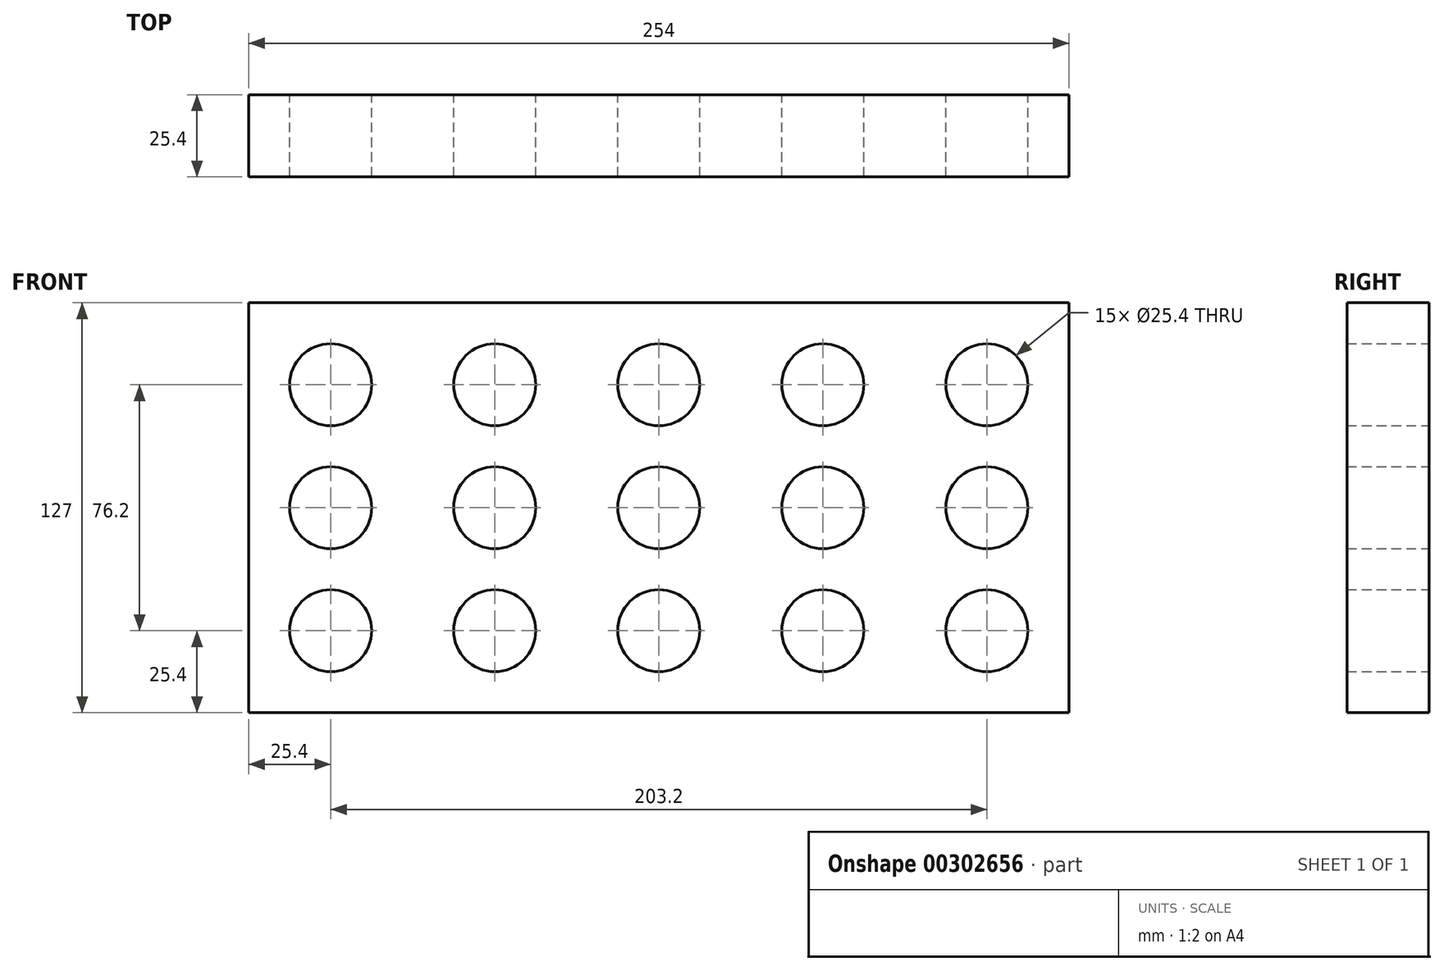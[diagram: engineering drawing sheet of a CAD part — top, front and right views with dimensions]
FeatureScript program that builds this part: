
annotation { "Feature Type Name" : "Feature", "Feature Type Description" : "" }
export const myFeature = defineFeature(function(context is Context, id is Id, definition is map)
    precondition{}
    {
        {
            var Q0;
            Q0=qCreatedBy(makeId("Front.planeOp"),FACE);
            var sketch = newSketch(context, id + "F0", { "sketchPlane" : qUnion([Q0])});
            skLineSegment(sketch, "E0.bottom", {"start": v(0, 0) * mm, "end": v(254, 0) * mm});
            skLineSegment(sketch, "E0.top", {"start": v(0, -127) * mm, "end": v(254, -127) * mm});
            skLineSegment(sketch, "E0.left", {"start": v(0, 0) * mm, "end": v(0, -127) * mm});
            skLineSegment(sketch, "E0.right", {"start": v(254, 0) * mm, "end": v(254, -127) * mm});
            skCircle(sketch, "E1", {"center": v(25.4, -25.4) * mm, "radius": 12.7 * mm});
            skCircle(sketch, "E2.0.1.0", {"center": v(25.4, -63.5) * mm, "radius": 12.7 * mm});
            skCircle(sketch, "E2.1.0.0", {"center": v(76.2, -25.4) * mm, "radius": 12.7 * mm});
            skCircle(sketch, "E2.1.1.0", {"center": v(76.2, -63.5) * mm, "radius": 12.7 * mm});
            skCircle(sketch, "E2.2.0.0", {"center": v(127, -25.4) * mm, "radius": 12.7 * mm});
            skCircle(sketch, "E2.2.1.0", {"center": v(127, -63.5) * mm, "radius": 12.7 * mm});
            skCircle(sketch, "E2.3.0.0", {"center": v(177.8, -25.4) * mm, "radius": 12.7 * mm});
            skCircle(sketch, "E2.3.1.0", {"center": v(177.8, -63.5) * mm, "radius": 12.7 * mm});
            skCircle(sketch, "E2.4.0.0", {"center": v(228.6, -25.4) * mm, "radius": 12.7 * mm});
            skCircle(sketch, "E2.4.1.0", {"center": v(228.6, -63.5) * mm, "radius": 12.7 * mm});
            skLineSegment(sketch, "E2.direction1", {"start": v(25.4, -25.4) * mm, "end": v(76.2, -25.4) * mm, "construction": true});
            skLineSegment(sketch, "E2.direction2", {"start": v(25.4, -25.4) * mm, "end": v(25.4, -63.5) * mm, "construction": true});
            skCircle(sketch, "E3.0.1.0", {"center": v(25.4, -101.6) * mm, "radius": 12.7 * mm});
            skCircle(sketch, "E3.1.1.0", {"center": v(76.2, -101.6) * mm, "radius": 12.7 * mm});
            skCircle(sketch, "E3.2.1.0", {"center": v(127, -101.6) * mm, "radius": 12.7 * mm});
            skCircle(sketch, "E3.3.1.0", {"center": v(177.8, -101.6) * mm, "radius": 12.7 * mm});
            skCircle(sketch, "E3.4.1.0", {"center": v(228.6, -101.6) * mm, "radius": 12.7 * mm});
            skLineSegment(sketch, "E3.direction1", {"start": v(38.1, -63.5) * mm, "end": v(88.9, -63.5) * mm, "construction": true});
            skLineSegment(sketch, "E3.direction2", {"start": v(38.1, -63.5) * mm, "end": v(38.1, -101.6) * mm, "construction": true});
            skSolve(sketch);
        }
        {
            var Q0;
            Q0=makeQuery(id+"F0.imprint","IMPRINT",FACE,{"disambiguationData":[TD([[makeQuery(id+"F0.imprint","IMPRINT",EDGE,{"derivedFrom":sQuery(id+"F0.wireOp",EDGE,"E0.bottom")}),-1.0]])]});
            extrude(context, id + "F1", {"entities" : qUnion([Q0]), "depth" : 25.4 * mm});
        }
    });
